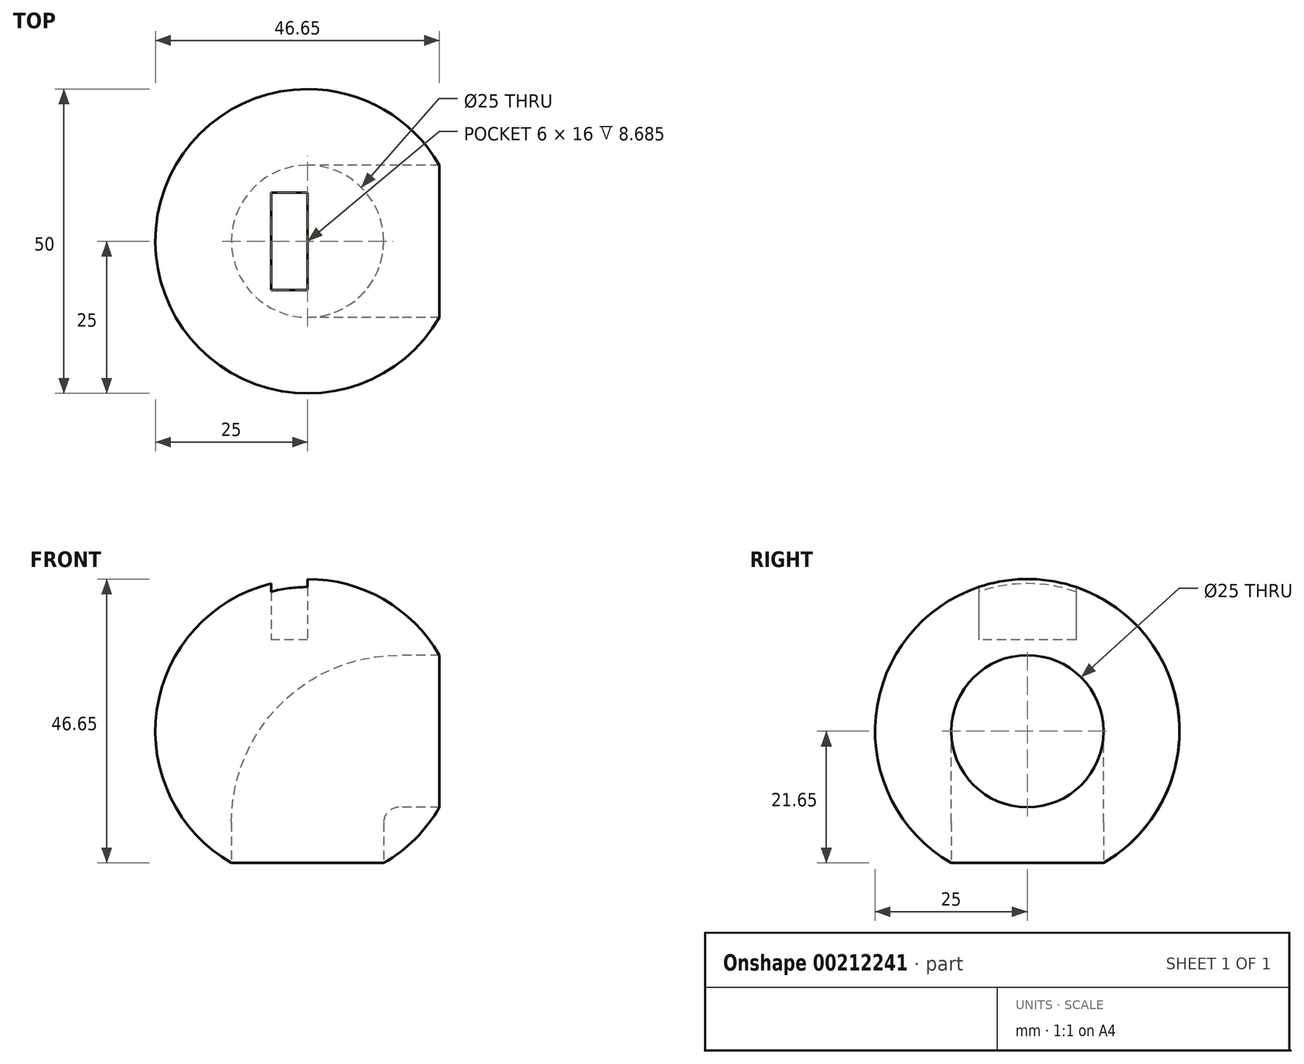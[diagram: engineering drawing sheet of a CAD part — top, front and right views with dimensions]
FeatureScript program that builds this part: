
annotation { "Feature Type Name" : "Feature", "Feature Type Description" : "" }
export const myFeature = defineFeature(function(context is Context, id is Id, definition is map)
    precondition{}
    {
        {
            var Q0;
            Q0=qCreatedBy(makeId("Right.planeOp"),FACE);
            var sketch = newSketch(context, id + "F0", { "sketchPlane" : qUnion([Q0])});
            skCircle(sketch, "E0", {"center": v(0, 0) * mm, "radius": 25 * mm});
            skLineSegment(sketch, "E1", {"start": v(0, 25) * mm, "end": v(0, -25) * mm});
            skSolve(sketch);
        }
        {
            var Q0;
            {var subQ0=sQuery(id+"F0.wireOp",EDGE,"E1");Q0=makeQuery(id+"F0.imprint","IMPRINT",FACE,{"disambiguationData":[TD([[makeQuery(id+"F0.imprint","IMPRINT",EDGE,{"derivedFrom":subQ0}),-1.0]])]});}
            var Q1;
            Q1=sQuery(id+"F0.wireOp",EDGE,"E1");
            revolve(context, id + "F1", {"entities" : qUnion([Q0]), "axis" : qUnion([Q1]), "revolveType" : RevolveType.FULL});
        }
        {
            var Q0;
            Q0=qCreatedBy(makeId("Right.planeOp"),FACE);
            cPlane(context, id + "F2", {"entities" : qUnion([Q0]), "cplaneType" : CPlaneType.OFFSET, "offset" : 25 * mm, "width" : 150 * mm, "height" : 150 * mm});
        }
        {
            var Q0;
            Q0=qCreatedBy(id+"F2.planeOp",FACE);
            var sketch = newSketch(context, id + "F3", { "sketchPlane" : qUnion([Q0])});
            skCircle(sketch, "E2", {"center": v(0, 0) * mm, "radius": 12.5 * mm});
            skSolve(sketch);
        }
        {
            var Q0;
            Q0=qCreatedBy(makeId("Front.planeOp"),FACE);
            var sketch = newSketch(context, id + "F4", { "sketchPlane" : qUnion([Q0])});
            skLineSegment(sketch, "E3", {"start": v(25, 0) * mm, "end": v(15, 0) * mm});
            skLineSegment(sketch, "E4", {"start": v(0, -15) * mm, "end": v(0, -25.97) * mm});
            skPoint(sketch, "E5.visualSharp", {"position": v(0, 0) * mm});
            skArc(sketch, "E5.filletArc", {"start": v(15, 0) * mm, "mid": v(4.4, -4.4) * mm, "end": v(0, -15) * mm});
            skLineSegment(sketch, "E6.bottom", {"start": v(0, 25) * mm, "end": v(-6, 25) * mm});
            skLineSegment(sketch, "E6.top", {"start": v(0, 15) * mm, "end": v(-6, 15) * mm});
            skLineSegment(sketch, "E6.left", {"start": v(0, 25) * mm, "end": v(0, 15) * mm});
            skLineSegment(sketch, "E6.right", {"start": v(-6, 25) * mm, "end": v(-6, 15) * mm});
            skSolve(sketch);
        }
        {
            var Q0;
            Q0=makeQuery(id+"F3.imprint","IMPRINT",FACE,{"disambiguationData":[TD([[makeQuery(id+"F3.imprint","IMPRINT",EDGE,{"derivedFrom":sQuery(id+"F3.wireOp",EDGE,"E2")}),1.0]])]});
            var Q1;
            Q1=sQuery(id+"F4.wireOp",EDGE,"E3");
            var Q2;
            Q2=sQuery(id+"F4.wireOp",EDGE,"E5.filletArc");
            var Q3;
            Q3=sQuery(id+"F4.wireOp",EDGE,"E4");
            sweep(context, id + "F5", {"operationType" : NewBodyOperationType.REMOVE, "profiles" : qUnion([Q0]), "path" : qUnion([Q1, Q2, Q3])});
        }
        {
            var Q0;
            Q0=makeQuery(id+"F4.imprint","IMPRINT",FACE,{"disambiguationData":[TD([[makeQuery(id+"F4.imprint","IMPRINT",EDGE,{"derivedFrom":sQuery(id+"F4.wireOp",EDGE,"E6.bottom")}),1.0]])]});
            extrude(context, id + "F6", {"entities" : qUnion([Q0]), "operationType" : NewBodyOperationType.REMOVE, "endBound" : BoundingType.SYMMETRIC, "oppositeDirection" : true, "depth" : 16 * mm});
        }
    });
